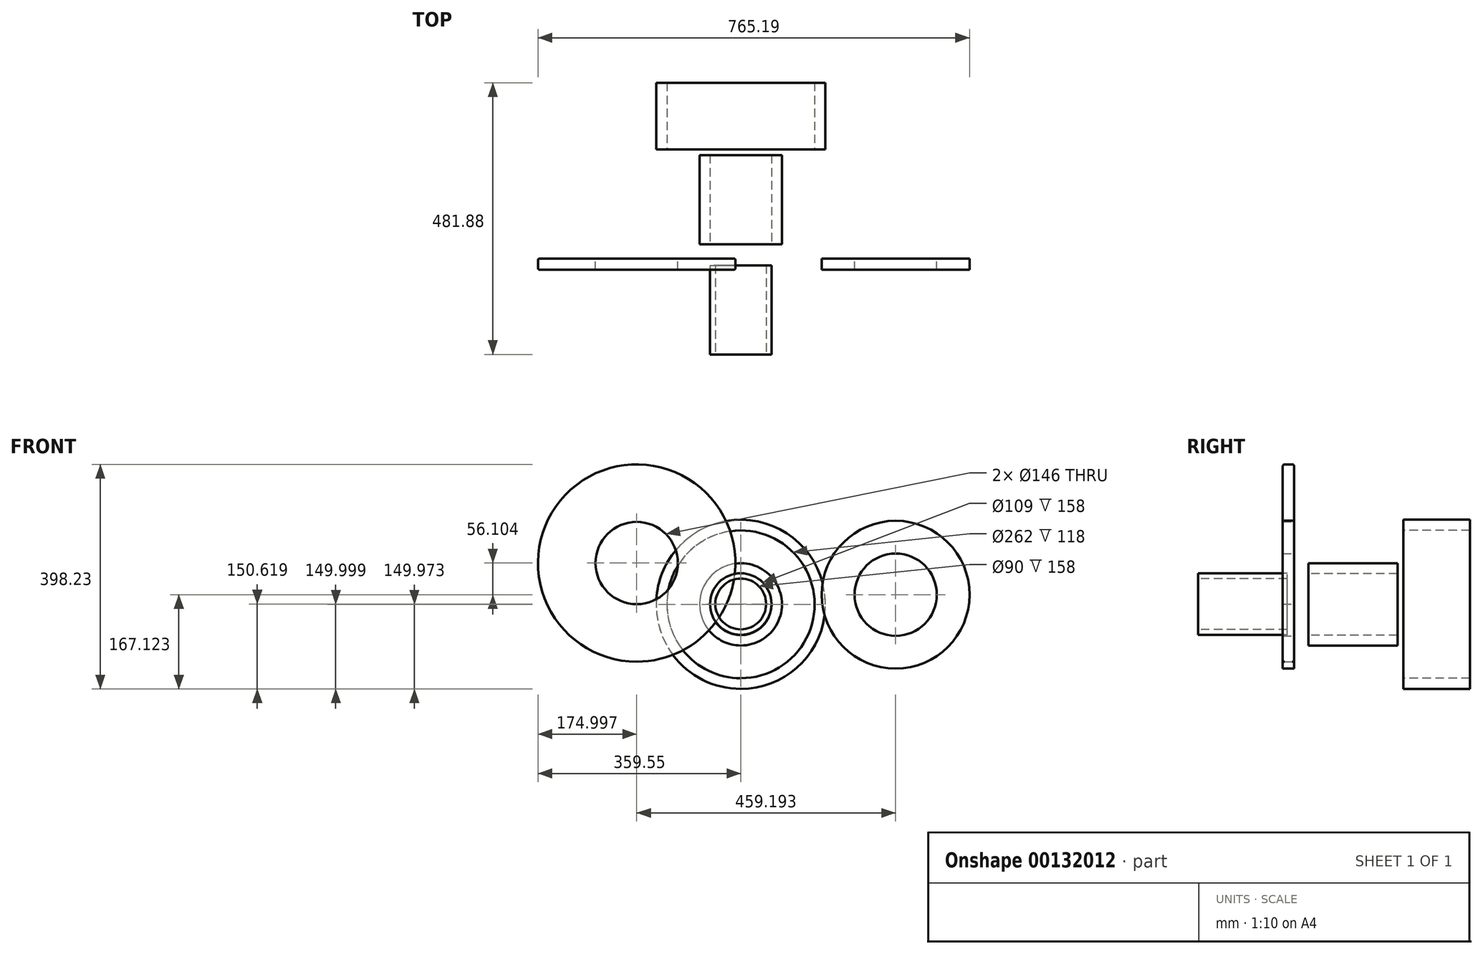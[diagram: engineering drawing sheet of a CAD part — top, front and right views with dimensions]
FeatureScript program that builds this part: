
annotation { "Feature Type Name" : "Feature", "Feature Type Description" : "" }
export const myFeature = defineFeature(function(context is Context, id is Id, definition is map)
    precondition{}
    {
        {
            var Q0;
            Q0=qCreatedBy(makeId("Right.planeOp"),FACE);
            var sketch = newSketch(context, id + "F0", { "sketchPlane" : qUnion([Q0])});
            skLineSegment(sketch, "E0.bottom", {"start": v(-170.22, -22.96) * mm, "end": v(-12.22, -22.96) * mm});
            skLineSegment(sketch, "E0.top", {"start": v(-170.22, -32.46) * mm, "end": v(-12.22, -32.46) * mm});
            skLineSegment(sketch, "E0.left", {"start": v(-170.22, -22.96) * mm, "end": v(-170.22, -32.46) * mm});
            skLineSegment(sketch, "E0.right", {"start": v(-12.22, -22.96) * mm, "end": v(-12.22, -32.46) * mm});
            skLineSegment(sketch, "E1", {"start": v(-170.22, -77.46) * mm, "end": v(-12.22, -77.46) * mm});
            skSolve(sketch);
        }
        {
            var Q0;
            Q0=qCreatedBy(makeId("Right.planeOp"),FACE);
            var sketch = newSketch(context, id + "F1", { "sketchPlane" : qUnion([Q0])});
            skLineSegment(sketch, "E2.bottom", {"start": v(25.36, -23.6) * mm, "end": v(183.36, -23.6) * mm});
            skLineSegment(sketch, "E2.top", {"start": v(25.36, -5.1) * mm, "end": v(183.36, -5.1) * mm});
            skLineSegment(sketch, "E2.left", {"start": v(25.36, -23.6) * mm, "end": v(25.36, -5.1) * mm});
            skLineSegment(sketch, "E2.right", {"start": v(183.36, -23.6) * mm, "end": v(183.36, -5.1) * mm});
            skLineSegment(sketch, "E3", {"start": v(25.36, -78.1) * mm, "end": v(183.36, -78.1) * mm});
            skSolve(sketch);
        }
        {
            var Q0;
            Q0=qCreatedBy(makeId("Right.planeOp"),FACE);
            var sketch = newSketch(context, id + "F2", { "sketchPlane" : qUnion([Q0])});
            skLineSegment(sketch, "E4.bottom", {"start": v(193.66, 71.92) * mm, "end": v(311.66, 71.92) * mm});
            skLineSegment(sketch, "E4.top", {"start": v(193.66, 52.92) * mm, "end": v(311.66, 52.92) * mm});
            skLineSegment(sketch, "E4.left", {"start": v(193.66, 71.92) * mm, "end": v(193.66, 52.92) * mm});
            skLineSegment(sketch, "E4.right", {"start": v(311.66, 71.92) * mm, "end": v(311.66, 52.92) * mm});
            skLineSegment(sketch, "E5", {"start": v(193.66, -78.08) * mm, "end": v(311.66, -78.08) * mm});
            skSolve(sketch);
        }
        {
            var Q0;
            Q0=qCreatedBy(makeId("Front.planeOp"),FACE);
            var sketch = newSketch(context, id + "F3", { "sketchPlane" : qUnion([Q0])});
            skCircle(sketch, "E6", {"center": v(-184.55, -4.85) * mm, "radius": 73 * mm});
            skCircle(sketch, "E7", {"center": v(-184.55, -4.85) * mm, "radius": 175 * mm});
            skSolve(sketch);
        }
        {
            var Q0;
            Q0=qCreatedBy(makeId("Front.planeOp"),FACE);
            var sketch = newSketch(context, id + "F4", { "sketchPlane" : qUnion([Q0])});
            skCircle(sketch, "E8", {"center": v(274.64, -60.96) * mm, "radius": 73 * mm});
            skCircle(sketch, "E9", {"center": v(274.64, -60.96) * mm, "radius": 131 * mm});
            skSolve(sketch);
        }
        {
            var Q0;
            Q0=makeQuery(id+"F3.imprint","IMPRINT",FACE,{"disambiguationData":[TD([[makeQuery(id+"F3.imprint","IMPRINT",EDGE,{"derivedFrom":sQuery(id+"F3.wireOp",EDGE,"E6")}),-1.0]])]});
            extrude(context, id + "F5", {"entities" : qUnion([Q0]), "depth" : 20 * mm});
        }
        {
            var Q0;
            Q0=makeQuery(id+"F4.imprint","IMPRINT",FACE,{"disambiguationData":[TD([[makeQuery(id+"F4.imprint","IMPRINT",EDGE,{"derivedFrom":sQuery(id+"F4.wireOp",EDGE,"E8")}),-1.0]])]});
            extrude(context, id + "F6", {"entities" : qUnion([Q0]), "depth" : 20 * mm});
        }
        {
            var Q0;
            Q0=makeQuery(id+"F0.imprint","IMPRINT",FACE,{"disambiguationData":[TD([[makeQuery(id+"F0.imprint","IMPRINT",EDGE,{"derivedFrom":sQuery(id+"F0.wireOp",EDGE,"E0.bottom")}),-1.0]])]});
            var Q1;
            Q1=sQuery(id+"F0.wireOp",EDGE,"E1");
            revolve(context, id + "F7", {"entities" : qUnion([Q0]), "axis" : qUnion([Q1]), "revolveType" : RevolveType.FULL});
        }
        {
            var Q0;
            Q0=makeQuery(id+"F1.imprint","IMPRINT",FACE,{"disambiguationData":[TD([[makeQuery(id+"F1.imprint","IMPRINT",EDGE,{"derivedFrom":sQuery(id+"F1.wireOp",EDGE,"E2.bottom")}),1.0]])]});
            var Q1;
            Q1=sQuery(id+"F1.wireOp",EDGE,"E3");
            revolve(context, id + "F8", {"entities" : qUnion([Q0]), "axis" : qUnion([Q1]), "revolveType" : RevolveType.FULL});
        }
        {
            var Q0;
            Q0=makeQuery(id+"F2.imprint","IMPRINT",FACE,{"disambiguationData":[TD([[makeQuery(id+"F2.imprint","IMPRINT",EDGE,{"derivedFrom":sQuery(id+"F2.wireOp",EDGE,"E4.bottom")}),-1.0]])]});
            var Q1;
            Q1=sQuery(id+"F2.wireOp",EDGE,"E5");
            revolve(context, id + "F9", {"entities" : qUnion([Q0]), "axis" : qUnion([Q1]), "revolveType" : RevolveType.FULL});
        }
        {
            var Q0;
            Q0=makeQuery(id+"F5.opExtrude","CAP_EDGE",EDGE,{"disambiguationData":[OSD([sQuery(id+"F3.wireOp",EDGE,"E7")])],"isStart":false});
            var Q1;
            Q1=makeQuery(id+"F5.opExtrude","CAP_EDGE",EDGE,{"disambiguationData":[OSD([sQuery(id+"F3.wireOp",EDGE,"E7")])],"isStart":true});
            fillet(context, id + "F10", {"entities" : qUnion([Q0, Q1]), "radius" : 3 * mm, "tangentPropagation" : true, "allowEdgeOverflow" : false});
        }
    });
